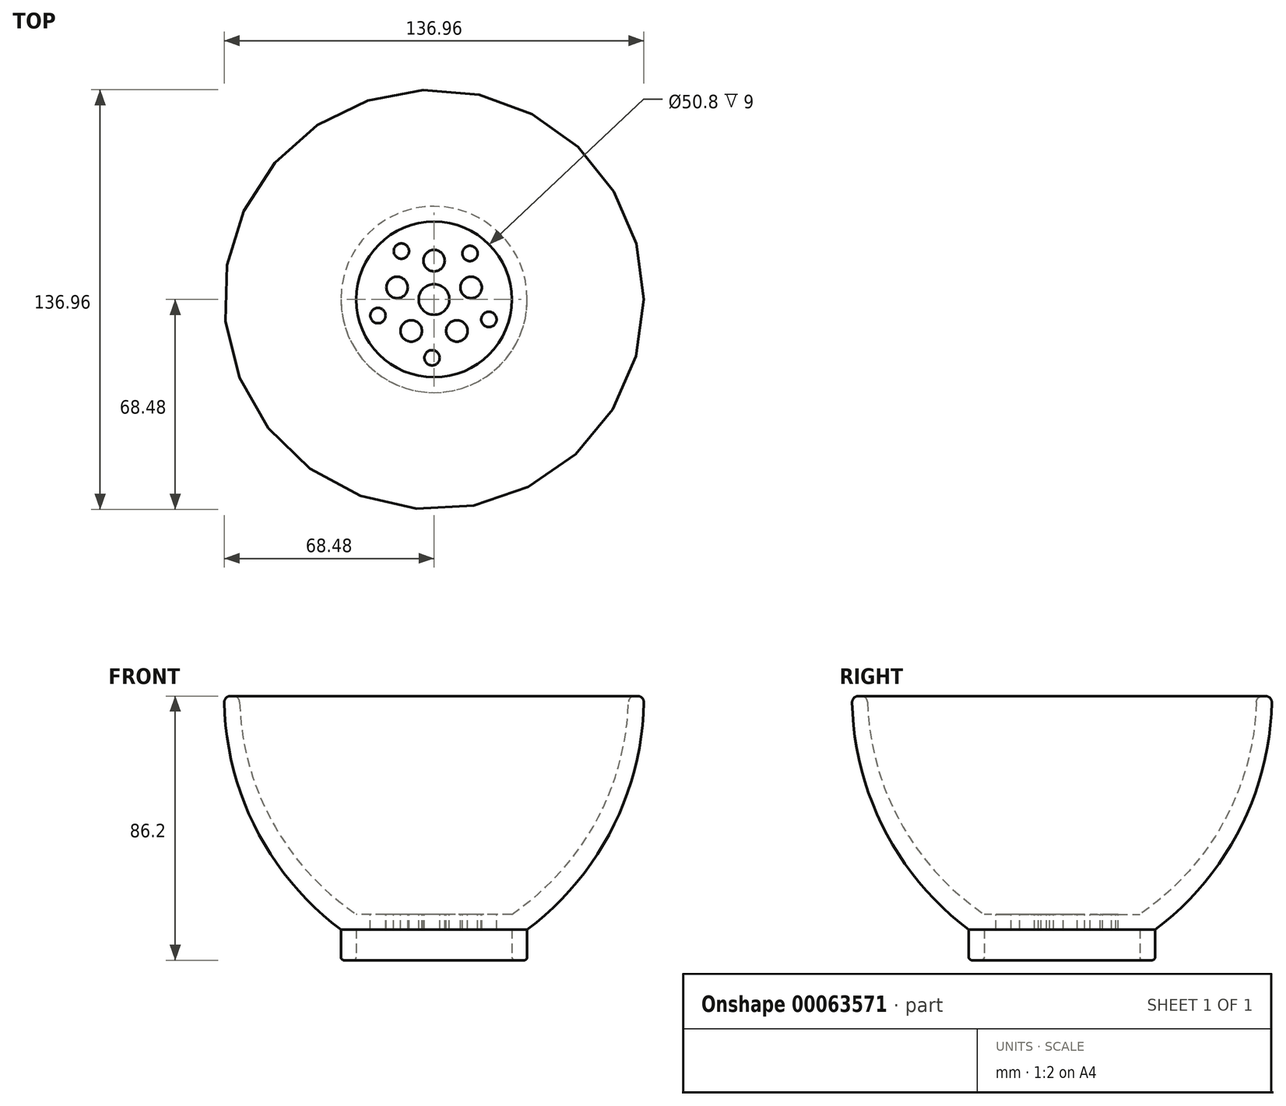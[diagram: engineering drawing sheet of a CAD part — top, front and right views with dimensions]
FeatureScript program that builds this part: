
annotation { "Feature Type Name" : "Feature", "Feature Type Description" : "" }
export const myFeature = defineFeature(function(context is Context, id is Id, definition is map)
    precondition{}
    {
        {
            var Q0;
            Q0=qCreatedBy(makeId("Front.planeOp"),FACE);
            var sketch = newSketch(context, id + "F0", { "sketchPlane" : qUnion([Q0])});
            skLineSegment(sketch, "E0", {"start": v(0, 0) * mm, "end": v(0, 55.88) * mm, "construction": true});
            skLineSegment(sketch, "E1", {"start": v(0, 0) * mm, "end": v(49.79, 0) * mm, "construction": true});
            skSolve(sketch);
        }
        {
            var Q0;
            Q0=qCreatedBy(makeId("Front.planeOp"),FACE);
            var sketch = newSketch(context, id + "F1", { "sketchPlane" : qUnion([Q0])});
            skLineSegment(sketch, "E2", {"start": v(0, 10) * mm, "end": v(25.4, 10) * mm});
            skLineSegment(sketch, "E3", {"start": v(30.4, 10) * mm, "end": v(30.4, 0) * mm});
            skLineSegment(sketch, "E4", {"start": v(25.4, 0) * mm, "end": v(30.4, 0) * mm});
            skLineSegment(sketch, "E5", {"start": v(25.4, 0) * mm, "end": v(25.4, 10) * mm});
            skLineSegment(sketch, "E6", {"start": v(0, 10) * mm, "end": v(0, 15) * mm});
            skLineSegment(sketch, "E7", {"start": v(0, 15) * mm, "end": v(25.4, 15) * mm});
            skLineSegment(sketch, "E8", {"start": v(0, 86.2) * mm, "end": v(127, 86.2) * mm, "construction": true});
            skArc(sketch, "E9", {"start": v(25.4, 15) * mm, "mid": v(53.22, 45.9) * mm, "end": v(63.5, 86.2) * mm});
            skArc(sketch, "E10", {"start": v(30.4, 10) * mm, "mid": v(58.46, 43.6) * mm, "end": v(68.5, 86.2) * mm});
            skLineSegment(sketch, "E11", {"start": v(68.5, 86.2) * mm, "end": v(63.5, 86.2) * mm});
            skSolve(sketch);
        }
        {
            var Q0;
            Q0=makeQuery(id+"F1.imprint","IMPRINT",FACE,{"disambiguationData":[TD([[makeQuery(id+"F1.imprint","IMPRINT",EDGE,{"derivedFrom":sQuery(id+"F1.wireOp",EDGE,"E2")}),1.0]])]});
            var Q1;
            Q1=sQuery(id+"F0.wireOp",EDGE,"E0");
            revolve(context, id + "F2", {"entities" : qUnion([Q0]), "axis" : qUnion([Q1]), "revolveType" : RevolveType.FULL});
        }
        {
            var Q0;
            Q0=makeQuery(id+"F2.opRevolve","SWEPT_FACE",FACE,{"disambiguationData":[OSD([sQuery(id+"F1.wireOp",EDGE,"E11")])]});
            fillet(context, id + "F3", {"entities" : qUnion([Q0]), "radius" : 2 * mm, "tangentPropagation" : true, "allowEdgeOverflow" : false});
        }
        {
            var Q0;
            Q0=makeQuery(id+"F2.opRevolve","SWEPT_FACE",FACE,{"disambiguationData":[OSD([sQuery(id+"F1.wireOp",EDGE,"E4")])]});
            fillet(context, id + "F4", {"entities" : qUnion([Q0]), "radius" : 1 * mm, "tangentPropagation" : true, "allowEdgeOverflow" : false});
        }
        {
            var Q0;
            Q0=makeQuery(id+"F2.opRevolve","SWEPT_FACE",FACE,{"disambiguationData":[OSD([sQuery(id+"F1.wireOp",EDGE,"E7")])]});
            var sketch = newSketch(context, id + "F5", { "sketchPlane" : qUnion([Q0])});
            skCircle(sketch, "E12", {"center": v(0, 0) * mm, "radius": 6.35 * mm, "construction": true});
            skCircle(sketch, "E13", {"center": v(0, 0) * mm, "radius": 12.7 * mm, "construction": true});
            skCircle(sketch, "E14", {"center": v(0, 0) * mm, "radius": 19.05 * mm, "construction": true});
            skLineSegment(sketch, "E15", {"start": v(0, 25.4) * mm, "end": v(0, -25.4) * mm, "construction": true});
            skLineSegment(sketch, "E16", {"start": v(0, 0) * mm, "end": v(-17.96, -17.96) * mm, "construction": true});
            skLineSegment(sketch, "E17", {"start": v(0, 0) * mm, "end": v(17.2, 18.7) * mm, "construction": true});
            skLineSegment(sketch, "E18", {"start": v(-17.96, 17.96) * mm, "end": v(0, 0) * mm, "construction": true});
            skLineSegment(sketch, "E19", {"start": v(0, 0) * mm, "end": v(18.7, -17.2) * mm, "construction": true});
            skSolve(sketch);
        }
        {
            var Q0;
            Q0=makeQuery(id+"F5.imprint","IMPRINT",FACE,{"disambiguationData":[TD([[makeQuery(id+"F5.imprint","IMPRINT",EDGE,{"derivedFrom":makeQuery(id+"F2.opRevolve","SWEPT_EDGE",EDGE,{"disambiguationData":[OSD([sQuery(id+"F1.wireOp",EDGE,"E7"),sQuery(id+"F1.wireOp",EDGE,"E9")])]})}),-1.0]])]});
            var sketch = newSketch(context, id + "F6", { "sketchPlane" : qUnion([Q0])});
            skCircle(sketch, "E20", {"center": v(0, 0) * mm, "radius": 5 * mm});
            skCircle(sketch, "E21", {"center": v(0, 12.7) * mm, "radius": 3.5 * mm});
            skCircle(sketch, "E22.1.0", {"center": v(-12.07, 3.92) * mm, "radius": 3.5 * mm});
            skCircle(sketch, "E22.2.0", {"center": v(-7.46, -10.27) * mm, "radius": 3.5 * mm});
            skCircle(sketch, "E22.3.0", {"center": v(7.46, -10.27) * mm, "radius": 3.5 * mm});
            skCircle(sketch, "E22.4.0", {"center": v(12.07, 3.92) * mm, "radius": 3.5 * mm});
            skCircle(sketch, "E23", {"center": v(-10.66, 15.8) * mm, "radius": 2.5 * mm});
            skCircle(sketch, "E24.1.0", {"center": v(-18.31, -5.25) * mm, "radius": 2.5 * mm});
            skCircle(sketch, "E24.2.0", {"center": v(-0.66, -19.04) * mm, "radius": 2.5 * mm});
            skCircle(sketch, "E24.3.0", {"center": v(17.9, -6.51) * mm, "radius": 2.5 * mm});
            skCircle(sketch, "E24.4.0", {"center": v(11.73, 15.01) * mm, "radius": 2.5 * mm});
            skSolve(sketch);
        }
        {
            var Q0;
            Q0 = qSketchRegion(id + "F6", true);
            var Q1;
            Q1=makeQuery(id+"F2.opRevolve","SWEPT_FACE",FACE,{"disambiguationData":[OSD([sQuery(id+"F1.wireOp",EDGE,"E2")])]});
            extrude(context, id + "F7", {"entities" : qUnion([Q0]), "operationType" : NewBodyOperationType.REMOVE, "endBound" : BoundingType.UP_TO_SURFACE, "oppositeDirection" : true, "endBoundEntityFace" : qUnion([Q1]), "depth" : 25.4 * mm});
        }
    });
